# Revit family: F1AE_2963-2962-2606_OS275
name_source: partatom
category: Finestre
units: mm (PartAtom-declared; Revit-internal decimal feet)

## family parameters
Condiviso = No
Host = Muro
Numero OmniClass = 23.30.20.00
Punto di calcolo locali = No
Sempre verticale = Sì
Taglio con vuoti quando caricato = No
Titolo OmniClass = Windows

## types (4) — shared parameters
Altezza = 1500 mm  [stored 4.92126 ft]
Altezza di default del davanzale = 800 mm
Chiusura muro = Per host
Costruzione analitica = <Nessuno>
Descrizione = Finestra 1 anta apertura esterna
H = 1500 mm  [stored 4.92126 ft]
H1 = 1500 mm  [stored 4.92126 ft]
H_Max = 2900 mm
H_Min = 450 mm
H_maniglia = 500 mm  [stored 1.64042 ft]
H_vetro = 1424 mm  [stored 4.67192 ft]
L_Max = 1000 mm  [stored 3.28084 ft]
L_Min = 400 mm  [stored 1.31234 ft]
Maniglia_alta = 1050 mm  [stored 3.44488 ft]
Maniglia_bassa = 750 mm
Maniglia_media = 500 mm  [stored 1.64042 ft]
Modello = OS2 75
Produttore = Secco Sistemi Spa
URL = https://www.seccosistemi.com
n2_cerniere = 2
n3_cerniere = 3
n4_cerniere = 4
numero_cerniere = 3
zero-valued in all types: H_fermavetro, L_fermavetro

## per-type parameters (varying)
| type | L | L1 | L_vetro | Larghezza | MATERIALE | WARNING |
| Acciaio zincato | 1000 mm  [stored 3.28084 ft] | 1000 mm  [stored 3.28084 ft] | 924 mm  [stored 3.0315 ft] | 1500 mm  [stored 4.92126 ft] | Acciaio | Sì |
| Acciaio inox | 1000 mm  [stored 3.28084 ft] | 1000 mm  [stored 3.28084 ft] | 924 mm  [stored 3.0315 ft] | 1500 mm  [stored 4.92126 ft] | Acciaio inox, spazzolato | Sì |
| Acciaio corten | 1000 mm  [stored 3.28084 ft] | 1000 mm  [stored 3.28084 ft] | 924 mm  [stored 3.0315 ft] | 1500 mm  [stored 4.92126 ft] | Acciaio corten | Sì |
| Ottone | 800 mm | 800 mm | 724 mm | 800 mm | Ottone | No |

note: [stored X ft] marks values corroborated as IEEE doubles in the binary element streams (Revit-internal decimal feet)
